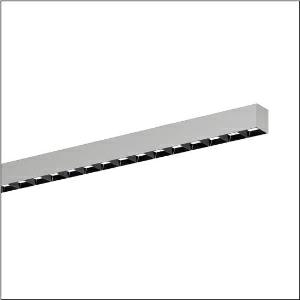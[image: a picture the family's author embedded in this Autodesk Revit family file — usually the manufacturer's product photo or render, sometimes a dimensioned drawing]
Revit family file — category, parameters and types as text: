
# Revit family: silica_r__21_51mx22dc4asb_d7c9
name_source: partatom
category: Lighting Fixtures
units: mm (PartAtom-declared; Revit-internal decimal feet)

## family parameters
Cut with Voids When Loaded = No
Host = Face
Light Source = No
Part Type = Normal
Room Calculation Point = No
Round Connector Dimension = Use Diameter
Shared = No

## types (1)
- --- (1 x LED, 10800 lm, 64.7 W, 4000K)
    Apparent Load = 65 VA
    CIE Flux Codes = 86 100 100 100 100
    Color Rendering = 80
    Color Temperature = 4000K
    Default Elevation = 1800 mm
    Description = Silica® 21, office luminaire, primary light control with darklight reflector, of PMMA, black, CAT 2 (L<= 3000cd/m²), light emission: direct distribution, primary light characteristic: symmetric, installation type: surface-mounted, LED, rated luminous flux: 10.800lm, luminous efficacy: 167lm/W, light colour: 840, colour temperature: 4000K, with terminal, 3+2-pole, max. 2.5mm², mains connection: 220..240V, AC, 50/60Hz, rated input power: 64.7W, luminaire housing, of aluminium, metallic grey (RAL 9006), length: 3.004mm, width: 53mm, height: 53mm, protection rating (complete): IP20, insulation class (complete): insulation class I (protective earthing), certification: CE, permissible operating ambient temperature: 0..+35°C, standard: EN 50419, packaging unit: 1 piece
    Height = 0 mm  [stored 0 ft]
    Lamp = 1 x LED
    Lamp Light Flux = 10800 lm
    Lamp Power = 64.7 W
    Lamp count = 1
    Length = 3004 mm
    Luminous efficacy = 167 lm/W
    Manufacturer = Siteco
    ModVariant = No
    Model = 51MX22DC4ASB
    Mounting Place = Ceiling
    Mounting Type = Recessed
    Number of Poles = 1
    OnlyDefault = Yes
    Power Factor = 1
    Product Name = Silica® 21
    Product group = office luminaire | ceiling recessed
    ProductGroupID = 400
    Protection Class = Protection class I
    Protection Degree = IP 20
    RLX_Detail_Level = 1
    RLX_Emergency_Light_Flux = 0 lm
    RLX_Emergency_Type = 0
    RLX_Emergency_Type_DB = No
    RlxData = <blob elided: 63025 chars, md5=3a611cda>
    Socket = socket
    Standby Power = 0 W
    System Light Flux = 10800 lm
    System Power = 65 W
    Type Comments = factory setting: luminous flux: 100 % | dim-lin: 254 | 366 mA
    Type Image = l_1335929.jpg
    URL = http://relux.com
    VarID = @adj_094637
    Voltage = 0 V
    Weight = 0.00 kg
    Width = 53 mm

note: [stored X ft] marks values corroborated as IEEE doubles in the binary element streams (Revit-internal decimal feet)

## geometry (parser evidence)
native form markers: Blend x4, Sweep x10
no freeform markers — native parametric forms only
